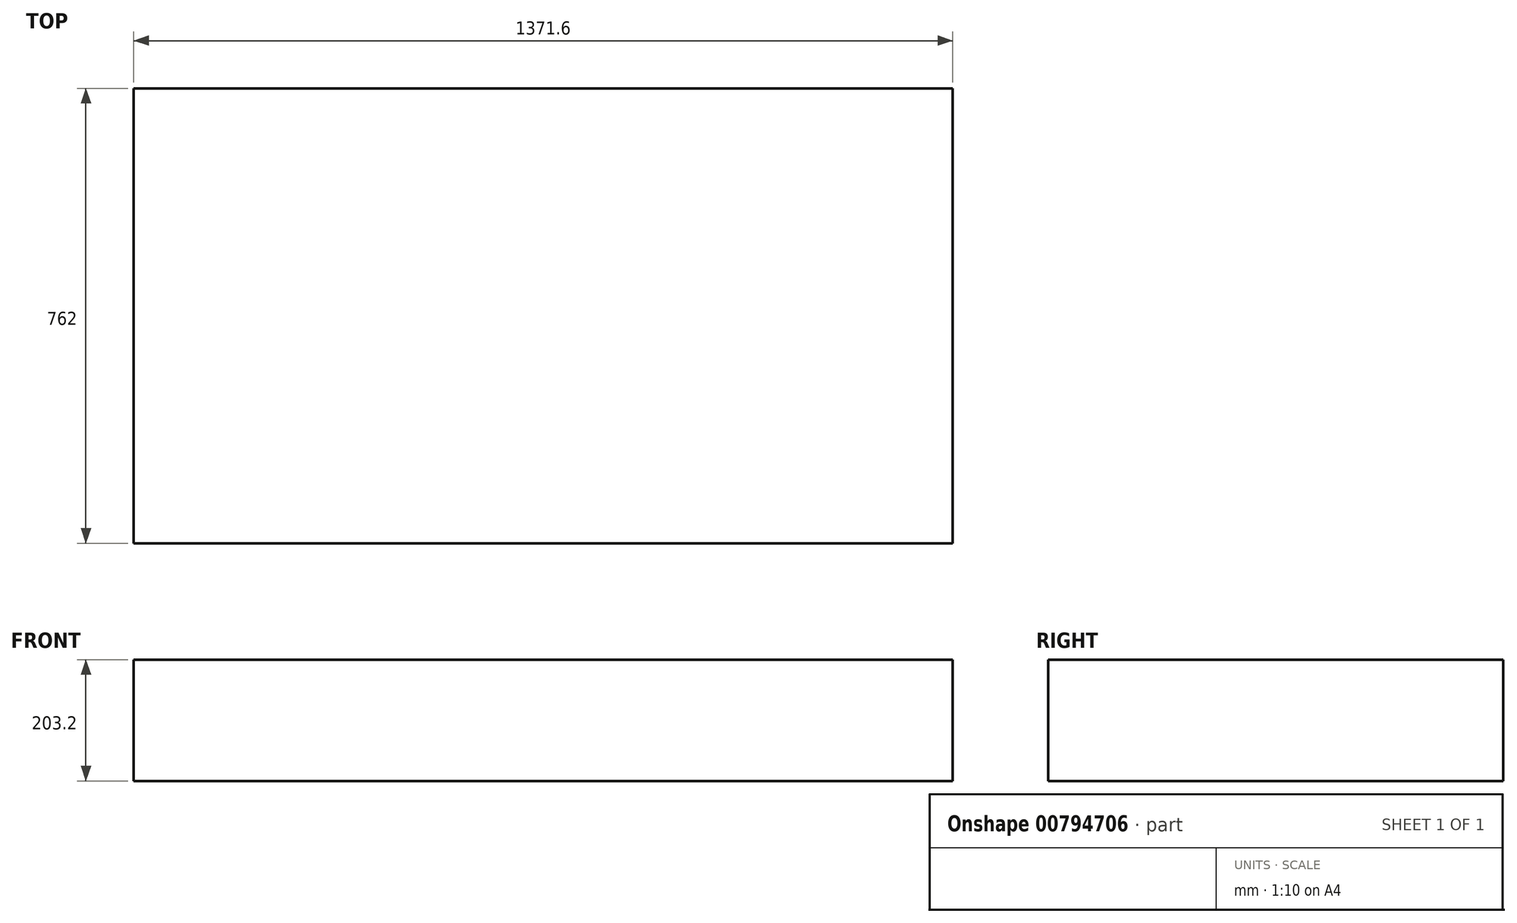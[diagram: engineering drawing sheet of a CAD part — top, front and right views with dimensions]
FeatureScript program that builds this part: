
annotation { "Feature Type Name" : "Feature", "Feature Type Description" : "" }
export const myFeature = defineFeature(function(context is Context, id is Id, definition is map)
    precondition{}
    {
        {
            var Q0;
            Q0=qCreatedBy(makeId("Top.planeOp"),FACE);
            var sketch = newSketch(context, id + "F0", { "sketchPlane" : qUnion([Q0])});
            skLineSegment(sketch, "E0.bottom", {"start": v(685.8, -381) * mm, "end": v(-685.8, -381) * mm});
            skLineSegment(sketch, "E0.top", {"start": v(685.8, 381) * mm, "end": v(-685.8, 381) * mm});
            skLineSegment(sketch, "E0.left", {"start": v(685.8, -381) * mm, "end": v(685.8, 381) * mm});
            skLineSegment(sketch, "E0.right", {"start": v(-685.8, -381) * mm, "end": v(-685.8, 381) * mm});
            skPoint(sketch, "E0.middle", {"position": v(0, 0) * mm});
            skSolve(sketch);
        }
        {
            var Q0;
            Q0=makeQuery(id+"F0.imprint","IMPRINT",FACE,{"disambiguationData":[TD([[makeQuery(id+"F0.imprint","IMPRINT",EDGE,{"derivedFrom":sQuery(id+"F0.wireOp",EDGE,"E0.bottom")}),-1.0]])]});
            extrude(context, id + "F1", {"entities" : qUnion([Q0]), "depth" : 203.2 * mm});
        }
    });
